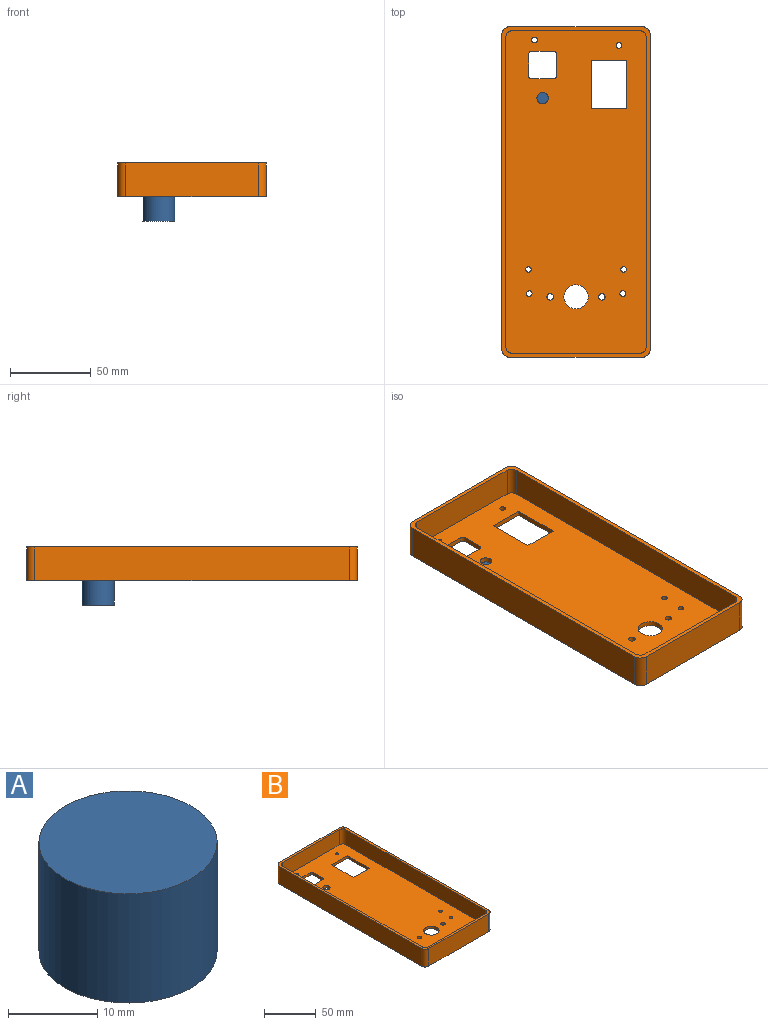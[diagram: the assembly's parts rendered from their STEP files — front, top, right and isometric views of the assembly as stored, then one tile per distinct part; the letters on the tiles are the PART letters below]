
ASSEMBLY  parts=2 mates=1
PART A: 3 faces, bbox 20x20x15 mm
  f0: cylinder r=10mm len=20mm, axis (0,0,1), area 942.5mm2, adj f1,f2
  f1: plane 20x20mm, normal (0,0,1), area 314.2mm2, adj f0
  f2: plane 20x20mm, normal (0,0,-1), area 314.2mm2, adj f0
PART B: 41 faces, bbox 92x205x21 mm
  f0: plane 200x87mm, normal (0,0,1), area 16134.1mm2, adj f10,f11,f12,f13,f14,f15,f16,f17
  f1: plane 195x21mm, normal (-1,0,0), area 4095mm2, adj f2,f8,f9,f18
  f2: cylinder r=5mm len=21mm, axis (0,0,1), area 164.9mm2, adj f1,f3,f9,f18
  f3: plane 82x21mm, normal (0,-1,0), area 1722mm2, adj f2,f4,f9,f18
  f4: cylinder r=5mm len=21mm, axis (0,0,1), area 164.9mm2, adj f3,f5,f9,f18
  f5: plane 195x21mm, normal (1,0,0), area 4095mm2, adj f4,f6,f9,f18
  f6: cylinder r=5mm len=21mm, axis (0,0,1), area 164.9mm2, adj f5,f7,f9,f18
  f7: plane 82x21mm, normal (0,1,0), area 1722mm2, adj f6,f8,f9,f18
  f8: cylinder r=5mm len=21mm, axis (0,0,1), area 164.9mm2, adj f1,f7,f9,f18
  f9: plane 205x92mm, normal (0,0,-1), area 17586.4mm2, adj f1,f2,f3,f4,f5,f6,f7,f8
  f10: cylinder r=4mm len=18mm, axis (0,0,1), area 113.1mm2, adj f0,f11,f17,f18
  f11: plane 192x18mm, normal (1,0,0), area 3456mm2, adj f0,f10,f12,f18
  f12: cylinder r=4mm len=18mm, axis (0,0,1), area 113.1mm2, adj f0,f11,f13,f18
  f13: plane 79x18mm, normal (0,-1,0), area 1422mm2, adj f0,f12,f14,f18
  f14: cylinder r=4mm len=18mm, axis (0,0,1), area 113.1mm2, adj f0,f13,f15,f18
  f15: plane 192x18mm, normal (-1,0,0), area 3456mm2, adj f0,f14,f16,f18
  f16: cylinder r=4mm len=18mm, axis (0,0,1), area 113.1mm2, adj f0,f15,f17,f18
  f17: plane 79x18mm, normal (0,1,0), area 1422mm2, adj f0,f10,f16,f18
  f18: plane 205x92mm, normal (0,0,1), area 1452.3mm2, adj f1,f2,f3,f4,f5,f6,f7,f8
  f19: cylinder r=3.5mm len=7mm, axis (0,0,1), area 66mm2, adj f0,f9
  f20: plane 22x3mm, normal (0,-1,0), area 66mm2, adj f0,f9,f21,f23
  f21: plane 30x3mm, normal (1,0,0), area 90mm2, adj f0,f9,f20,f22
  f22: plane 22x3mm, normal (0,1,0), area 66mm2, adj f0,f9,f21,f23
  f23: plane 30x3mm, normal (-1,0,0), area 90mm2, adj f0,f9,f20,f22
  f24: cylinder r=1.75mm len=3.5mm, axis (0,0,1), area 33mm2, adj f0,f9
  f25: cylinder r=1.75mm len=3.5mm, axis (0,0,1), area 33mm2, adj f0,f9
  f26: cylinder r=2mm len=4mm, axis (0,0,1), area 37.7mm2, adj f0,f9
  f27: cylinder r=7.5mm len=15mm, axis (0,0,1), area 141.4mm2, adj f0,f9
  f28: cylinder r=2mm len=4mm, axis (0,0,1), area 37.7mm2, adj f0,f9
  f29: cylinder r=1.75mm len=3.5mm, axis (0,0,1), area 33mm2, adj f0,f9
  f30: cylinder r=2mm len=3mm, axis (0,0,1), area 9.4mm2, adj f0,f9,f31,f37
  f31: plane 13x3mm, normal (1,0,0), area 39mm2, adj f0,f9,f30,f32
  f32: cylinder r=2mm len=3mm, axis (0,0,1), area 9.4mm2, adj f0,f9,f31,f33
  f33: plane 13.5x3mm, normal (0,1,0), area 40.5mm2, adj f0,f9,f32,f34
  f34: cylinder r=2mm len=3mm, axis (0,0,1), area 9.4mm2, adj f0,f9,f33,f35
  f35: plane 13x3mm, normal (-1,0,0), area 39mm2, adj f0,f9,f34,f36
  f36: cylinder r=2mm len=3mm, axis (0,0,1), area 9.4mm2, adj f0,f9,f35,f37
  f37: plane 13.5x3mm, normal (0,-1,0), area 40.5mm2, adj f0,f9,f30,f36
  f38: cylinder r=1.75mm len=3.5mm, axis (0,0,1), area 33mm2, adj f0,f9
  f39: cylinder r=1.75mm len=3.5mm, axis (0,0,1), area 33mm2, adj f0,f9
  f40: cylinder r=1.75mm len=3.5mm, axis (0,0,1), area 33mm2, adj f0,f9
PLACE A rot(axis=(1,0,0),180deg) t=(-23.52,73.71,-4.89)mm
PLACE B t=(-2.82,15.51,-4.89)mm
MATE fastened A.f0 <-> B.f19  axis (0,0,1) through (-23.52,73.71,-4.89)mm
